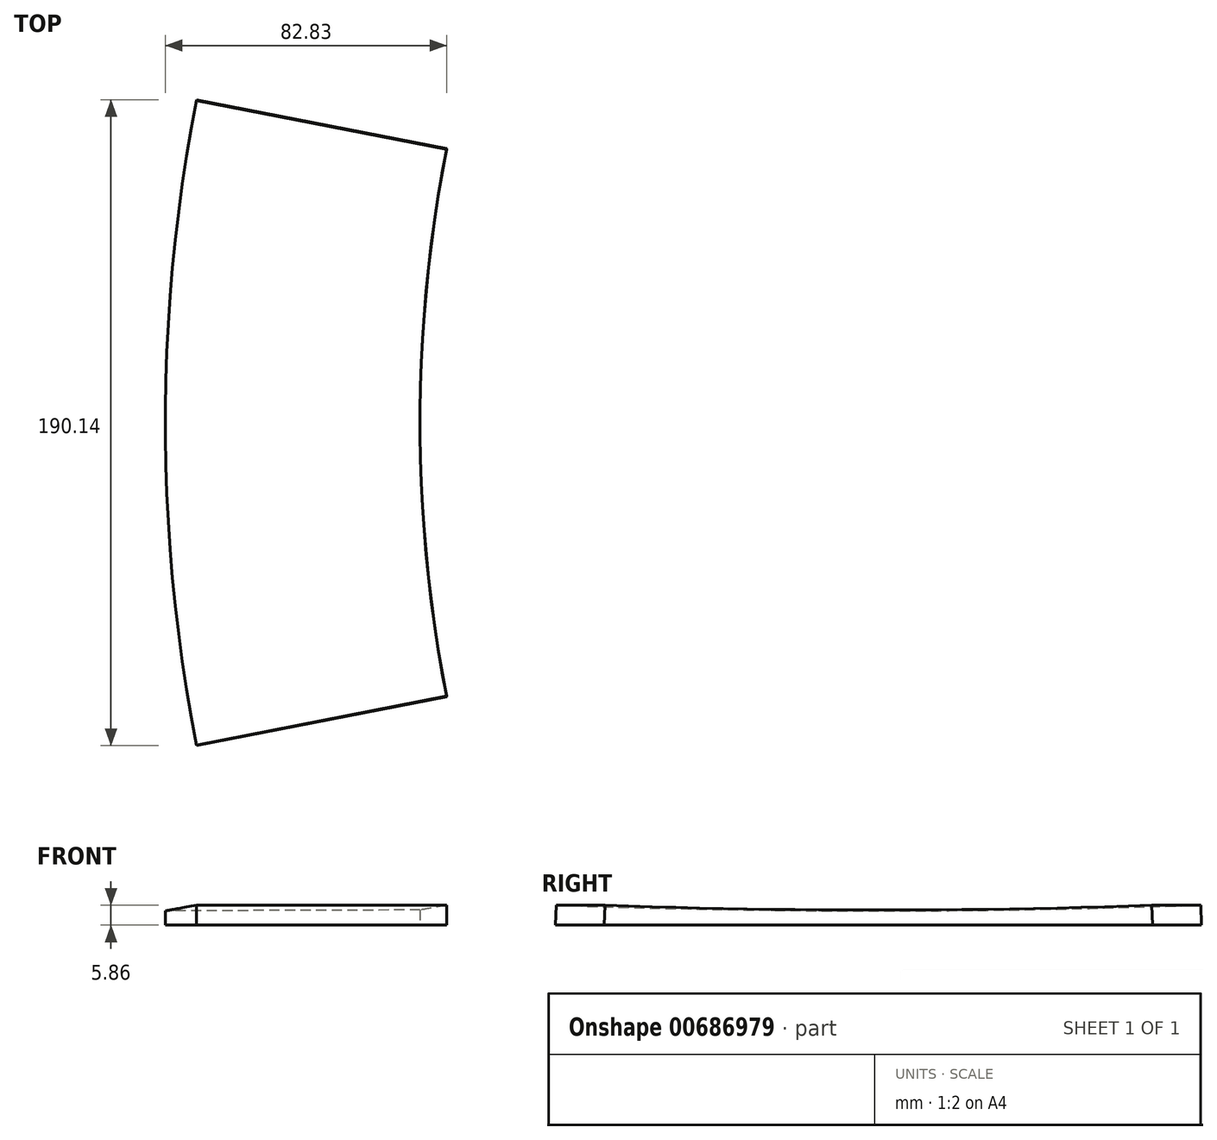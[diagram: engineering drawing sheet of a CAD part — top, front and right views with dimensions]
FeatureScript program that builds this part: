
annotation { "Feature Type Name" : "Feature", "Feature Type Description" : "" }
export const myFeature = defineFeature(function(context is Context, id is Id, definition is map)
    precondition{}
    {
        {
            var Q0;
            Q0=qCreatedBy(makeId("Front.planeOp"),FACE);
            var sketch = newSketch(context, id + "F0", { "sketchPlane" : qUnion([Q0])});
            skLineSegment(sketch, "E0", {"start": v(-0.07, -1.79) * mm, "end": v(534.04, 0) * mm});
            skLineSegment(sketch, "E1", {"start": v(534.04, 0) * mm, "end": v(517.63, 91.28) * mm});
            skLineSegment(sketch, "E2", {"start": v(517.63, 91.28) * mm, "end": v(-0.07, -1.79) * mm});
            skLineSegment(sketch, "E3", {"start": v(517.63, 91.28) * mm, "end": v(479.74, 302.03) * mm});
            skLineSegment(sketch, "E4", {"start": v(479.74, 302.03) * mm, "end": v(-37.96, 208.96) * mm});
            skArc(sketch, "E5", {"start": v(-37.96, 208.96) * mm, "mid": v(-26.34, 158.67) * mm, "end": v(-9.85, 109.75) * mm});
            skLineSegment(sketch, "E6", {"start": v(-9.85, 109.75) * mm, "end": v(479.74, 302.03) * mm});
            skLineSegment(sketch, "E7", {"start": v(-9.85, 109.75) * mm, "end": v(9.88, 0) * mm});
            skLineSegment(sketch, "E8", {"start": v(-0.07, -1.79) * mm, "end": v(0, -21.79) * mm});
            skLineSegment(sketch, "E9", {"start": v(0, -21.79) * mm, "end": v(156, -21.27) * mm});
            skLineSegment(sketch, "E10", {"start": v(156, -21.27) * mm, "end": v(155.93, -1.27) * mm});
            skLineSegment(sketch, "E11.bottom", {"start": v(40.44, -2.59) * mm, "end": v(115.44, -2.34) * mm});
            skLineSegment(sketch, "E11.top", {"start": v(40.5, -21.65) * mm, "end": v(115.5, -21.4) * mm});
            skLineSegment(sketch, "E11.left", {"start": v(40.44, -2.59) * mm, "end": v(40.5, -21.65) * mm});
            skLineSegment(sketch, "E11.right", {"start": v(115.44, -2.34) * mm, "end": v(115.5, -21.4) * mm});
            skSolve(sketch);
        }
        {
            var Q0;
            Q0=makeQuery(id+"F0.imprint","IMPRINT",FACE,{"disambiguationData":[TD([[makeQuery(id+"F0.imprint","IMPRINT",EDGE,{"derivedFrom":sQuery(id+"F0.wireOp",EDGE,"E11.bottom")}),-1.0]])]});
            var Q1;
            Q1=sQuery(id+"F0.wireOp",EDGE,"E1");
            revolve(context, id + "F1", {"entities" : qUnion([Q0]), "axis" : qUnion([Q1]), "revolveType" : RevolveType.SYMMETRIC, "angle" : 22.5 * degree});
        }
        {
            var Q0;
            Q0=qCreatedBy(makeId("Front.planeOp"),FACE);
            var sketch = newSketch(context, id + "F2", { "sketchPlane" : qUnion([Q0])});
            skLineSegment(sketch, "E12.bottom", {"start": v(27.48, -6.8) * mm, "end": v(140.54, -6.8) * mm});
            skLineSegment(sketch, "E12.top", {"start": v(27.48, -31.15) * mm, "end": v(140.54, -31.15) * mm});
            skLineSegment(sketch, "E12.left", {"start": v(27.48, -6.8) * mm, "end": v(27.48, -31.15) * mm});
            skLineSegment(sketch, "E12.right", {"start": v(140.54, -6.8) * mm, "end": v(140.54, -31.15) * mm});
            skSolve(sketch);
        }
        {
            var Q0;
            Q0=makeQuery(id+"F2.imprint","IMPRINT",FACE,{"disambiguationData":[TD([[makeQuery(id+"F2.imprint","IMPRINT",EDGE,{"derivedFrom":sQuery(id+"F2.wireOp",EDGE,"E12.bottom")}),-1.0]])]});
            extrude(context, id + "F3", {"entities" : qUnion([Q0]), "operationType" : NewBodyOperationType.REMOVE, "endBound" : BoundingType.SYMMETRIC, "depth" : 240 * mm, "offsetDistance" : 25 * mm});
        }
    });
